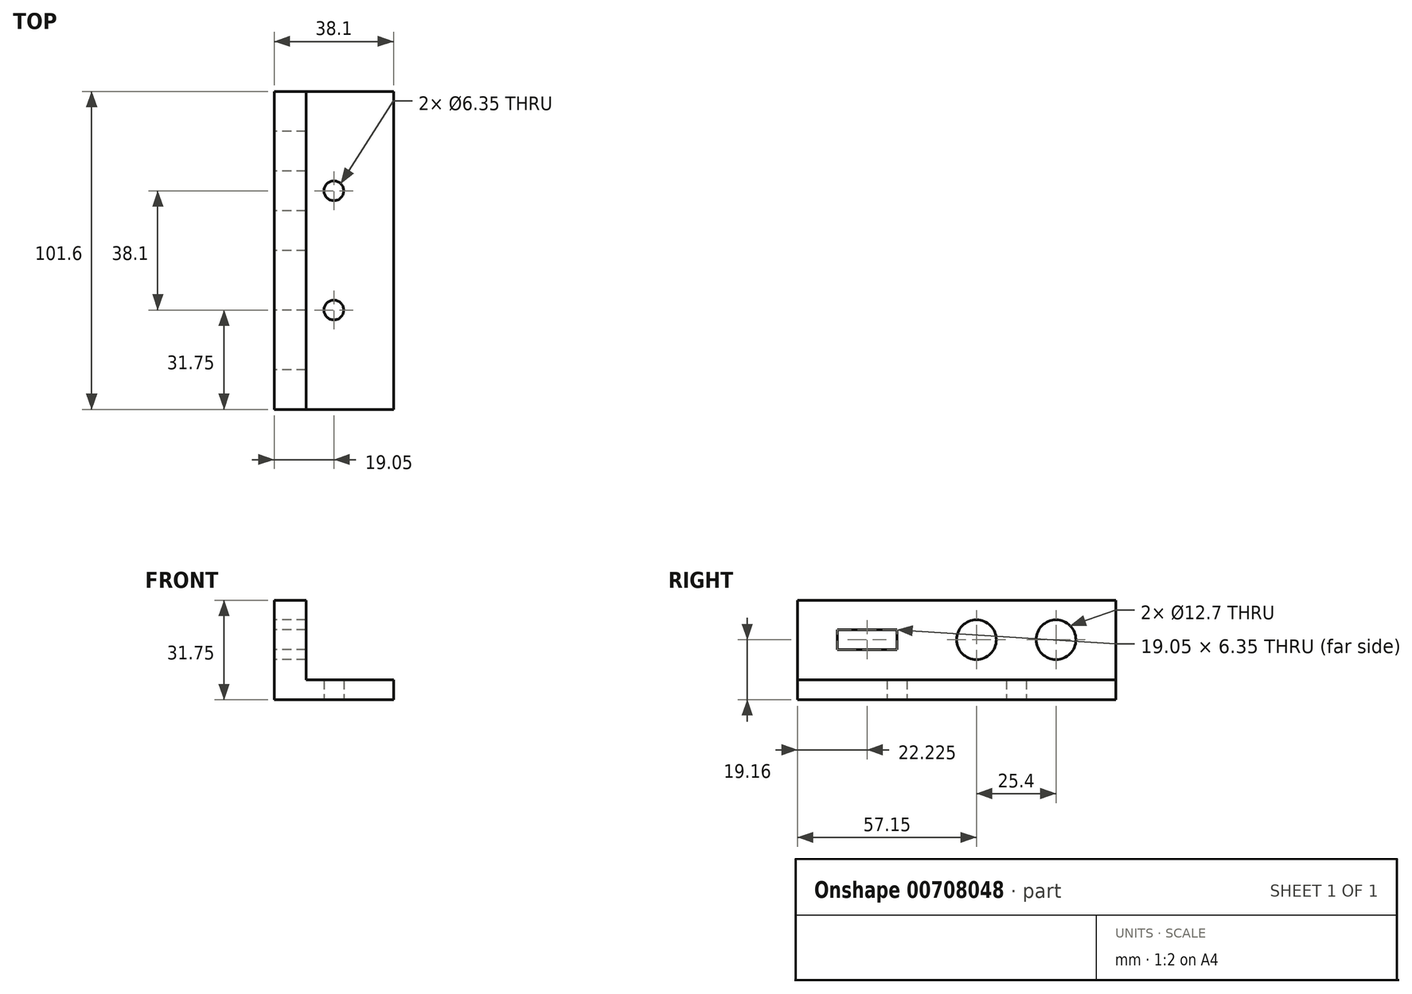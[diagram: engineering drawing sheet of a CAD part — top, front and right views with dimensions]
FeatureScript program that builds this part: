
annotation { "Feature Type Name" : "Feature", "Feature Type Description" : "" }
export const myFeature = defineFeature(function(context is Context, id is Id, definition is map)
    precondition{}
    {
        {
            var Q0;
            Q0=qCreatedBy(makeId("Top.planeOp"),FACE);
            var sketch = newSketch(context, id + "F0", { "sketchPlane" : qUnion([Q0])});
            skLineSegment(sketch, "E0.bottom", {"start": v(0, 0) * mm, "end": v(38.1, 0) * mm});
            skLineSegment(sketch, "E0.top", {"start": v(0, 101.6) * mm, "end": v(38.1, 101.6) * mm});
            skLineSegment(sketch, "E0.left", {"start": v(0, 0) * mm, "end": v(0, 101.6) * mm});
            skLineSegment(sketch, "E0.right", {"start": v(38.1, 0) * mm, "end": v(38.1, 101.6) * mm});
            skLineSegment(sketch, "E1", {"start": v(19.05, 101.6) * mm, "end": v(19.05, 69.85) * mm, "construction": true});
            skLineSegment(sketch, "E2", {"start": v(19.05, 0) * mm, "end": v(19.05, 31.75) * mm, "construction": true});
            skCircle(sketch, "E3", {"center": v(19.05, 69.85) * mm, "radius": 3.18 * mm});
            skCircle(sketch, "E4", {"center": v(19.05, 31.75) * mm, "radius": 3.18 * mm});
            skSolve(sketch);
        }
        {
            var Q0;
            Q0=makeQuery(id+"F0.imprint","IMPRINT",FACE,{"disambiguationData":[TD([[makeQuery(id+"F0.imprint","IMPRINT",EDGE,{"derivedFrom":sQuery(id+"F0.wireOp",EDGE,"E0.bottom")}),1.0]])]});
            extrude(context, id + "F1", {"entities" : qUnion([Q0]), "depth" : 6.35 * mm, "offsetDistance" : 25.4 * mm});
        }
        {
            var Q0;
            Q0=makeQuery(id+"F1.opExtrude","CAP_FACE",FACE,{"disambiguationData":[OSD([sQuery(id+"F0.wireOp",EDGE,"E0.bottom"),sQuery(id+"F0.wireOp",EDGE,"E0.top"),sQuery(id+"F0.wireOp",EDGE,"E0.left"),sQuery(id+"F0.wireOp",EDGE,"E0.right"),sQuery(id+"F0.wireOp",EDGE,"E3"),sQuery(id+"F0.wireOp",EDGE,"E4")])],"isStart":false});
            var sketch = newSketch(context, id + "F2", { "sketchPlane" : qUnion([Q0])});
            skLineSegment(sketch, "E5.bottom", {"start": v(0, 101.6) * mm, "end": v(10.16, 101.6) * mm});
            skLineSegment(sketch, "E5.top", {"start": v(0, 0) * mm, "end": v(10.16, 0) * mm});
            skLineSegment(sketch, "E5.left", {"start": v(0, 101.6) * mm, "end": v(0, 0) * mm});
            skLineSegment(sketch, "E5.right", {"start": v(10.16, 101.6) * mm, "end": v(10.16, 0) * mm});
            skSolve(sketch);
        }
        {
            var Q0;
            Q0=makeQuery(id+"F2.imprint","IMPRINT",FACE,{"disambiguationData":[TD([[makeQuery(id+"F2.imprint","IMPRINT",EDGE,{"derivedFrom":sQuery(id+"F2.wireOp",EDGE,"E5.bottom")}),-1.0]])]});
            extrude(context, id + "F3", {"entities" : qUnion([Q0]), "operationType" : NewBodyOperationType.ADD, "depth" : 25.4 * mm, "offsetDistance" : 25.4 * mm});
        }
        {
            var Q0;
            Q0=makeQuery(id+"F3.boolean.opBoolean","MERGE",FACE,{"derivedFrom":[makeQuery(id+"F1.opExtrude","SWEPT_FACE",FACE,{"disambiguationData":[OSD([sQuery(id+"F0.wireOp",EDGE,"E0.left")])]}),makeQuery(id+"F3.opExtrude","SWEPT_FACE",FACE,{"disambiguationData":[OSD([sQuery(id+"F2.wireOp",EDGE,"E5.left")])]})]});
            var sketch = newSketch(context, id + "F4", { "sketchPlane" : qUnion([Q0])});
            skCircle(sketch, "E6", {"center": v(-82.55, 19.16) * mm, "radius": 6.35 * mm});
            skCircle(sketch, "E7", {"center": v(-57.15, 19.16) * mm, "radius": 6.35 * mm});
            skLineSegment(sketch, "E8.top", {"start": v(-31.75, 15.99) * mm, "end": v(-12.7, 15.99) * mm});
            skLineSegment(sketch, "E8.left", {"start": v(-31.75, 19.16) * mm, "end": v(-31.75, 15.99) * mm});
            skLineSegment(sketch, "E8.right", {"start": v(-12.7, 19.16) * mm, "end": v(-12.7, 15.99) * mm});
            skLineSegment(sketch, "E9.top", {"start": v(-31.75, 22.34) * mm, "end": v(-12.7, 22.34) * mm});
            skLineSegment(sketch, "E9.left", {"start": v(-31.75, 19.16) * mm, "end": v(-31.75, 22.34) * mm});
            skLineSegment(sketch, "E9.right", {"start": v(-12.7, 19.16) * mm, "end": v(-12.7, 22.34) * mm});
            skSolve(sketch);
        }
        {
            var Q0;
            Q0=makeQuery(id+"F4.imprint","IMPRINT",FACE,{"disambiguationData":[TD([[makeQuery(id+"F4.imprint","IMPRINT",EDGE,{"derivedFrom":sQuery(id+"F4.wireOp",EDGE,"E6")}),1.0]])]});
            var Q1;
            Q1=makeQuery(id+"F4.imprint","IMPRINT",FACE,{"disambiguationData":[TD([[makeQuery(id+"F4.imprint","IMPRINT",EDGE,{"derivedFrom":sQuery(id+"F4.wireOp",EDGE,"E7")}),1.0]])]});
            var Q2;
            Q2=makeQuery(id+"F4.imprint","IMPRINT",FACE,{"disambiguationData":[TD([[makeQuery(id+"F4.imprint","IMPRINT",EDGE,{"derivedFrom":sQuery(id+"F4.wireOp",EDGE,"E8.top")}),1.0]])]});
            extrude(context, id + "F5", {"entities" : qUnion([Q0, Q1, Q2]), "operationType" : NewBodyOperationType.REMOVE, "oppositeDirection" : true, "depth" : 25.4 * mm, "offsetDistance" : 25.4 * mm});
        }
    });
